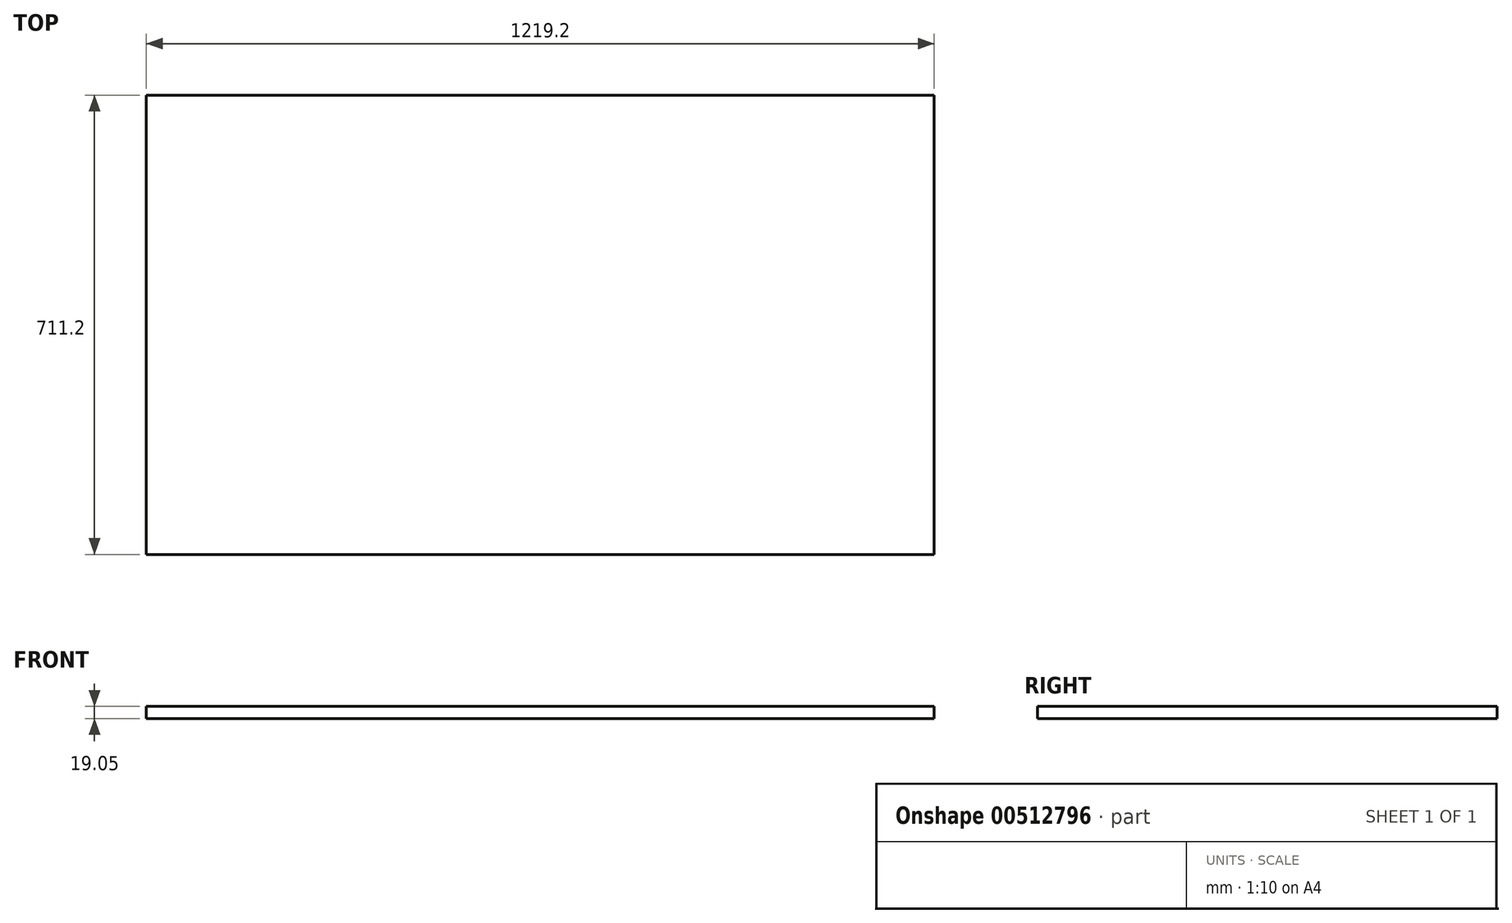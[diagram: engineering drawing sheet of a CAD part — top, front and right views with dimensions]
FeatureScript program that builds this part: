
annotation { "Feature Type Name" : "Feature", "Feature Type Description" : "" }
export const myFeature = defineFeature(function(context is Context, id is Id, definition is map)
    precondition{}
    {
        {
            var Q0;
            Q0=qCreatedBy(makeId("Top.planeOp"),FACE);
            var sketch = newSketch(context, id + "F0", { "sketchPlane" : qUnion([Q0])});
            skLineSegment(sketch, "E0.bottom", {"start": v(609.6, 355.6) * mm, "end": v(-609.6, 355.6) * mm});
            skLineSegment(sketch, "E0.top", {"start": v(609.6, -355.6) * mm, "end": v(-609.6, -355.6) * mm});
            skLineSegment(sketch, "E0.left", {"start": v(609.6, 355.6) * mm, "end": v(609.6, -355.6) * mm});
            skLineSegment(sketch, "E0.right", {"start": v(-609.6, 355.6) * mm, "end": v(-609.6, -355.6) * mm});
            skPoint(sketch, "E0.middle", {"position": v(0, 0) * mm});
            skSolve(sketch);
        }
        {
            var Q0;
            Q0=makeQuery(id+"F0.imprint","IMPRINT",FACE,{"disambiguationData":[TD([[makeQuery(id+"F0.imprint","IMPRINT",EDGE,{"derivedFrom":sQuery(id+"F0.wireOp",EDGE,"E0.bottom")}),1.0]])]});
            extrude(context, id + "F1", {"entities" : qUnion([Q0]), "depth" : 19.05 * mm});
        }
    });
